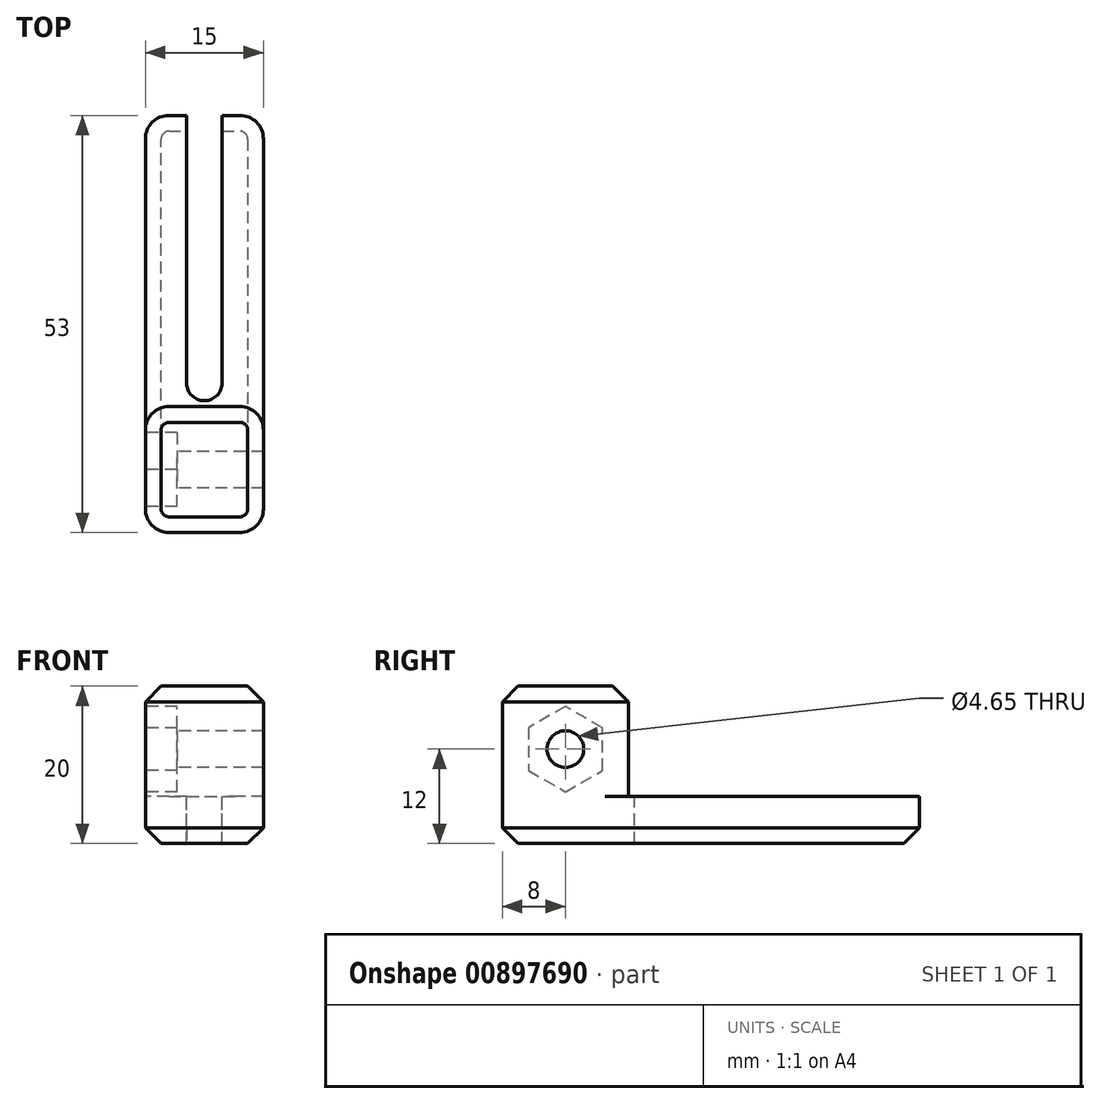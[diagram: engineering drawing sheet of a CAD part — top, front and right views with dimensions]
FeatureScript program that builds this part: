
annotation { "Feature Type Name" : "Feature", "Feature Type Description" : "" }
export const myFeature = defineFeature(function(context is Context, id is Id, definition is map)
    precondition{}
    {
        {
            var Q0;
            Q0=qCreatedBy(makeId("Top.planeOp"),FACE);
            var sketch = newSketch(context, id + "F0", { "sketchPlane" : qUnion([Q0])});
            skLineSegment(sketch, "E0.left", {"start": v(-45.11, -8) * mm, "end": v(-45.11, 45) * mm});
            skPoint(sketch, "E0.middle", {"position": v(0, 0) * mm});
            skLineSegment(sketch, "E1", {"start": v(0, 61.15) * mm, "end": v(0, -61.68) * mm, "construction": true});
            skLineSegment(sketch, "E2", {"start": v(66.79, 0) * mm, "end": v(-73.86, 0) * mm, "construction": true});
            skPoint(sketch, "E3.visualSharp", {"position": v(-45.11, 21.25) * mm});
            skPoint(sketch, "E4.visualSharp", {"position": v(-45.11, -21.37) * mm});
            skPoint(sketch, "E5.visualSharp", {"position": v(45.11, 21.37) * mm});
            skPoint(sketch, "E6.endSnap0", {"position": v(48.82, 14.43) * mm});
            skLineSegment(sketch, "E7", {"start": v(-45.11, -8) * mm, "end": v(-60.11, -8) * mm});
            skPoint(sketch, "E8.orphan", {"position": v(-35.53, -8) * mm});
            skPoint(sketch, "E9.orphan", {"position": v(48.82, 36.85) * mm});
            skPoint(sketch, "E6.end.orphan", {"position": v(48.82, -8) * mm});
            skLineSegment(sketch, "E10", {"start": v(-45.11, 45) * mm, "end": v(-60.11, 45) * mm});
            skLineSegment(sketch, "E11", {"start": v(-60.11, -8) * mm, "end": v(-60.11, 45) * mm});
            skSolve(sketch);
        }
        {
            var Q0;
            Q0=qSketchRegion(id+"F0",true);
            extrude(context, id + "F1", {"entities" : qUnion([Q0]), "depth" : 6 * mm, "offsetDistance" : 25 * mm});
        }
        {
            var Q0;
            Q0=makeQuery(id+"F1.opExtrude","CAP_FACE",FACE,{"disambiguationData":[OSD([sQuery(id+"F0.wireOp",EDGE,"E0.bottom"),sQuery(id+"F0.wireOp",EDGE,"E0.top"),sQuery(id+"F0.wireOp",EDGE,"E0.left"),sQuery(id+"F0.wireOp",EDGE,"E0.right"),sQuery(id+"F0.wireOp",EDGE,"E3.filletArc"),sQuery(id+"F0.wireOp",EDGE,"E4.filletArc"),sQuery(id+"F0.wireOp",EDGE,"f45c8361-92ba-424a-9424-ba666b682f90.filletArc"),sQuery(id+"F0.wireOp",EDGE,"E5.filletArc"),sQuery(id+"F0.wireOp",EDGE,"a7b3f125-5707-4f32-a8d1-9d9079d3b77c.0"),sQuery(id+"F0.wireOp",EDGE,"a7b3f125-5707-4f32-a8d1-9d9079d3b77c.1"),sQuery(id+"F0.wireOp",EDGE,"a7b3f125-5707-4f32-a8d1-9d9079d3b77c.2"),sQuery(id+"F0.wireOp",EDGE,"a7b3f125-5707-4f32-a8d1-9d9079d3b77c.3"),sQuery(id+"F0.wireOp",EDGE,"a7b3f125-5707-4f32-a8d1-9d9079d3b77c.4"),sQuery(id+"F0.wireOp",EDGE,"a7b3f125-5707-4f32-a8d1-9d9079d3b77c.5"),sQuery(id+"F0.wireOp",EDGE,"a7b3f125-5707-4f32-a8d1-9d9079d3b77c.6"),sQuery(id+"F0.wireOp",EDGE,"a7b3f125-5707-4f32-a8d1-9d9079d3b77c.7")])],"isStart":false});
            var sketch = newSketch(context, id + "F2", { "sketchPlane" : qUnion([Q0])});
            skLineSegment(sketch, "E12", {"start": v(0, -25) * mm, "end": v(0, 25) * mm, "construction": true});
            skPoint(sketch, "E12.startSnap0", {"position": v(0, -25) * mm});
            skPoint(sketch, "E12.endSnap0", {"position": v(0, 25) * mm});
            skLineSegment(sketch, "E13", {"start": v(-60.11, 0) * mm, "end": v(50, 0) * mm, "construction": true});
            skLineSegment(sketch, "E14", {"start": v(-60.11, 0) * mm, "end": v(-60.11, 8) * mm});
            skLineSegment(sketch, "E15", {"start": v(-60.11, 8) * mm, "end": v(-45.11, 8) * mm});
            skLineSegment(sketch, "E16", {"start": v(-45.11, 8) * mm, "end": v(-45.11, -8) * mm});
            skLineSegment(sketch, "E17", {"start": v(-45.11, -8) * mm, "end": v(-60.11, -8) * mm});
            skLineSegment(sketch, "E18", {"start": v(-60.11, -8) * mm, "end": v(-60.11, 0) * mm});
            skPoint(sketch, "E19.orphan", {"position": v(45.11, -8) * mm});
            skPoint(sketch, "E20.MirrorCS.end.orphan", {"position": v(60.11, -8) * mm});
            skPoint(sketch, "E21.MirrorCS.end.orphan", {"position": v(60.11, 0) * mm});
            skPoint(sketch, "E22.MirrorCS.end.orphan", {"position": v(45.11, 8) * mm});
            skPoint(sketch, "E22.MirrorCS.start.orphan", {"position": v(60.11, 8) * mm});
            skSolve(sketch);
        }
        {
            var Q0;
            Q0=qSketchRegion(id+"F2",true);
            extrude(context, id + "F3", {"entities" : qUnion([Q0]), "operationType" : NewBodyOperationType.ADD, "depth" : 14 * mm, "offsetDistance" : 25 * mm});
        }
        {
            var Q0;
            Q0=makeQuery(id+"F3.boolean.opBoolean","MERGE",FACE,{"derivedFrom":[makeQuery(id+"F1.opExtrude","SWEPT_FACE",FACE,{"disambiguationData":[OSD([sQuery(id+"F0.wireOp",EDGE,"a7b3f125-5707-4f32-a8d1-9d9079d3b77c.4")])]}),makeQuery(id+"F3.opExtrude","SWEPT_FACE",FACE,{"disambiguationData":[OSD([sQuery(id+"F2.wireOp",EDGE,"E14"),sQuery(id+"F2.wireOp",EDGE,"E18")])]})]});
            var sketch = newSketch(context, id + "F4", { "sketchPlane" : qUnion([Q0])});
            skLineSegment(sketch, "E23", {"start": v(0, 20) * mm, "end": v(0, 3) * mm, "construction": true});
            skCircle(sketch, "E24", {"center": v(0, 12) * mm, "radius": 2.33 * mm});
            skSolve(sketch);
        }
        {
            var Q0;
            Q0=makeQuery(id+"F4.imprint","IMPRINT",FACE,{"disambiguationData":[TD([[makeQuery(id+"F4.imprint","IMPRINT",EDGE,{"derivedFrom":sQuery(id+"F4.wireOp",EDGE,"E24")}),1.0]])]});
            var Q1;
            Q1=sQuery(id+"F4.wireOp",EDGE,"E24");
            extrude(context, id + "F5", {"entities" : qUnion([Q0]), "operationType" : NewBodyOperationType.REMOVE, "surfaceEntities" : qUnion([Q1]), "oppositeDirection" : true, "depth" : 25 * mm, "offsetDistance" : 25 * mm});
        }
        {
            var Q0;
            {var subQ0=sQuery(id+"F0.wireOp",EDGE,"E7");var subQ1=sQuery(id+"F0.wireOp",EDGE,"E11");var subQ2=sQuery(id+"F0.wireOp",EDGE,"E0.left");Q0=makeQuery(id+"F3.boolean.opBoolean","SPLIT",FACE,{"disambiguationData":[TD([makeQuery(id+"F1.opExtrude","SWEPT_FACE",FACE,{"disambiguationData":[OSD([subQ0])]})])],"derivedFrom":makeQuery(id+"F1.opExtrude","CAP_FACE",FACE,{"disambiguationData":[OSD([subQ2,subQ0,sQuery(id+"F0.wireOp",EDGE,"E10"),subQ1])],"isStart":false})});}
            var sketch = newSketch(context, id + "F6", { "sketchPlane" : qUnion([Q0])});
            skLineSegment(sketch, "E25", {"start": v(-52.61, -21.26) * mm, "end": v(-52.61, 89.89) * mm, "construction": true});
            skArc(sketch, "E26", {"start": v(-54.86, 11) * mm, "mid": v(-52.61, 8.75) * mm, "end": v(-50.36, 11) * mm});
            skLineSegment(sketch, "E27", {"start": v(-59.16, 11) * mm, "end": v(-47.5, 11) * mm, "construction": true});
            skLineSegment(sketch, "E28", {"start": v(-50.36, 11) * mm, "end": v(-50.36, 45) * mm});
            skLineSegment(sketch, "E29", {"start": v(-54.86, 11) * mm, "end": v(-54.86, 45) * mm});
            skLineSegment(sketch, "E30.0", {"start": v(-50.36, 45) * mm, "end": v(-54.86, 45) * mm});
            skPoint(sketch, "E31.orphan", {"position": v(-60.11, 45) * mm});
            skPoint(sketch, "E32.orphan", {"position": v(-45.11, 45) * mm});
            skSolve(sketch);
        }
        {
            var Q0;
            Q0 = qSketchRegion(id + "F6", true);
            extrude(context, id + "F7", {"entities" : qUnion([Q0]), "operationType" : NewBodyOperationType.REMOVE, "oppositeDirection" : true, "depth" : 25 * mm, "offsetDistance" : 25 * mm});
        }
        {
            var Q0;
            Q0=makeQuery(id+"F1.opExtrude","SWEPT_EDGE",EDGE,{"disambiguationData":[OSD([sQuery(id+"F0.wireOp",EDGE,"E0.left"),sQuery(id+"F0.wireOp",EDGE,"E7")])]});
            var Q1;
            Q1=makeQuery(id+"F1.opExtrude","SWEPT_EDGE",EDGE,{"disambiguationData":[OSD([sQuery(id+"F0.wireOp",EDGE,"E7"),sQuery(id+"F0.wireOp",EDGE,"E11")])]});
            var Q2;
            Q2=makeQuery(id+"F1.opExtrude","SWEPT_EDGE",EDGE,{"disambiguationData":[OSD([sQuery(id+"F0.wireOp",EDGE,"E0.left"),sQuery(id+"F0.wireOp",EDGE,"E10")])]});
            var Q3;
            Q3=makeQuery(id+"F1.opExtrude","SWEPT_EDGE",EDGE,{"disambiguationData":[OSD([sQuery(id+"F0.wireOp",EDGE,"E10"),sQuery(id+"F0.wireOp",EDGE,"E11")])]});
            fillet(context, id + "F8", {"entities" : qUnion([Q0, Q1, Q2, Q3]), "radius" : 3 * mm, "tangentPropagation" : true, "allowEdgeOverflow" : false});
        }
        {
            var Q0;
            Q0=makeQuery(id+"F1.opExtrude","CAP_EDGE",EDGE,{"disambiguationData":[OSD([sQuery(id+"F0.wireOp",EDGE,"E0.left")])],"isStart":true});
            var Q1;
            Q1=makeQuery(id+"F1.opExtrude","CAP_EDGE",EDGE,{"disambiguationData":[OSD([sQuery(id+"F0.wireOp",EDGE,"E11")])],"isStart":true});
            chamfer(context, id + "F9", {"entities" : qUnion([Q0, Q1]), "width" : 2 * mm, "tangentPropagation" : true});
        }
        {
            var Q0;
            Q0=makeQuery(id+"F3.boolean.opBoolean","MERGE",FACE,{"derivedFrom":[makeQuery(id+"F1.opExtrude","SWEPT_FACE",FACE,{"disambiguationData":[OSD([sQuery(id+"F0.wireOp",EDGE,"E11")])]}),makeQuery(id+"F3.opExtrude","SWEPT_FACE",FACE,{"disambiguationData":[OSD([sQuery(id+"F2.wireOp",EDGE,"E14"),sQuery(id+"F2.wireOp",EDGE,"E18")])]})]});
            var sketch = newSketch(context, id + "F10", { "sketchPlane" : qUnion([Q0])});
            skLineSegment(sketch, "E33", {"start": v(0, 23.38) * mm, "end": v(0, -3.64) * mm, "construction": true});
            skCircle(sketch, "E34.cCircle", {"center": v(0, 12) * mm, "radius": 4.7 * mm, "construction": true});
            skLineSegment(sketch, "E34.0", {"start": v(-4.7, 14.71) * mm, "end": v(0, 17.43) * mm});
            skLineSegment(sketch, "E34.1", {"start": v(0, 17.43) * mm, "end": v(4.7, 14.71) * mm});
            skLineSegment(sketch, "E34.2", {"start": v(4.7, 14.71) * mm, "end": v(4.7, 9.29) * mm});
            skLineSegment(sketch, "E34.3", {"start": v(4.7, 9.29) * mm, "end": v(0, 6.57) * mm});
            skLineSegment(sketch, "E34.4", {"start": v(0, 6.57) * mm, "end": v(-4.7, 9.29) * mm});
            skLineSegment(sketch, "E34.5", {"start": v(-4.7, 9.29) * mm, "end": v(-4.7, 14.71) * mm});
            skPoint(sketch, "E34.0.midPoint", {"position": v(-2.35, 16.07) * mm});
            skSolve(sketch);
        }
        {
            var Q0;
            Q0=makeQuery(id+"F10.imprint","IMPRINT",FACE,{"disambiguationData":[TD([[makeQuery(id+"F10.imprint","IMPRINT",EDGE,{"derivedFrom":sQuery(id+"F10.wireOp",EDGE,"E34.0")}),-1.0]])]});
            extrude(context, id + "F11", {"entities" : qUnion([Q0]), "operationType" : NewBodyOperationType.REMOVE, "oppositeDirection" : true, "depth" : 4 * mm, "offsetDistance" : 25 * mm});
        }
        {
            var Q0;
            Q0=makeQuery(id+"F3.opExtrude","CAP_EDGE",EDGE,{"disambiguationData":[OSD([sQuery(id+"F2.wireOp",EDGE,"E17")])],"isStart":false});
            cPoint(context, id + "F12", {"entities" : qUnion([Q0]), "parameter" : 0.5});
        }
        {
            var Q0;
            Q0=makeQuery(id+"F3.boolean.opBoolean","MERGE",FACE,{"derivedFrom":[makeQuery(id+"F1.opExtrude","SWEPT_FACE",FACE,{"disambiguationData":[OSD([sQuery(id+"F0.wireOp",EDGE,"E0.left")])]}),makeQuery(id+"F3.opExtrude","SWEPT_FACE",FACE,{"disambiguationData":[OSD([sQuery(id+"F2.wireOp",EDGE,"E16")])]})]});
            var Q1;
            Q1 = qCreatedBy(id + "F12" ,VERTEX);
            cPlane(context, id + "F13", {"entities" : qUnion([Q0, Q1]), "cplaneType" : CPlaneType.PLANE_POINT, "offset" : 26.3 * mm, "oppositeDirection" : true, "width" : 150 * mm, "height" : 150 * mm});
        }
        {
            var Q0;
            Q0=makeQuery(id+"F3.opExtrude","SWEPT_EDGE",EDGE,{"disambiguationData":[OSD([sQuery(id+"F0.wireOp",EDGE,"E0.left"),sQuery(id+"F2.wireOp",EDGE,"E16"),sQuery(id+"F2.wireOp",EDGE,"E17")])]});
            var Q1;
            Q1=makeQuery(id+"F3.opExtrude","SWEPT_EDGE",EDGE,{"disambiguationData":[OSD([sQuery(id+"F0.wireOp",EDGE,"E0.left"),sQuery(id+"F2.wireOp",EDGE,"E15"),sQuery(id+"F2.wireOp",EDGE,"E16")])]});
            var Q2;
            Q2=makeQuery(id+"F3.opExtrude","SWEPT_EDGE",EDGE,{"disambiguationData":[OSD([sQuery(id+"F0.wireOp",EDGE,"E11"),sQuery(id+"F2.wireOp",EDGE,"E17"),sQuery(id+"F2.wireOp",EDGE,"E18")])]});
            var Q3;
            Q3=makeQuery(id+"F3.opExtrude","SWEPT_EDGE",EDGE,{"disambiguationData":[OSD([sQuery(id+"F0.wireOp",EDGE,"E11"),sQuery(id+"F2.wireOp",EDGE,"E14"),sQuery(id+"F2.wireOp",EDGE,"E15")])]});
            fillet(context, id + "F14", {"entities" : qUnion([Q0, Q1, Q2, Q3]), "radius" : 3 * mm, "tangentPropagation" : true, "allowEdgeOverflow" : false});
        }
        {
            var Q0;
            Q0=makeQuery(id+"F3.opExtrude","CAP_EDGE",EDGE,{"disambiguationData":[OSD([sQuery(id+"F2.wireOp",EDGE,"E16")])],"isStart":false});
            chamfer(context, id + "F15", {"entities" : qUnion([Q0]), "width" : 2 * mm, "tangentPropagation" : true});
        }
    });
